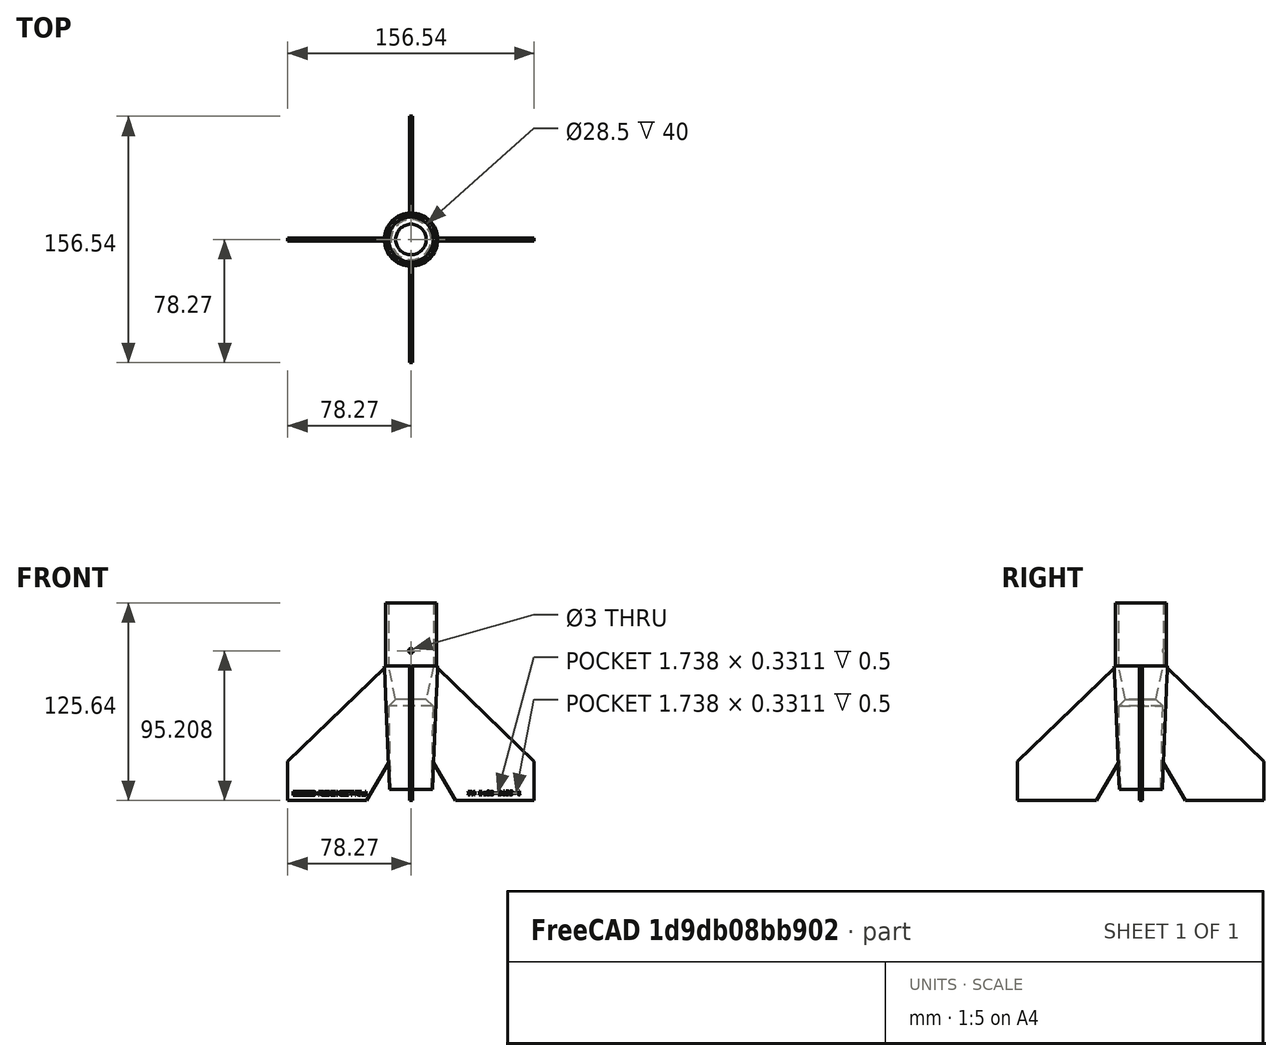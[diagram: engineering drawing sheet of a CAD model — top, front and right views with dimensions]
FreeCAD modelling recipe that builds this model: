
FCSTD DOCUMENT  (FreeCAD 0.20R29603 (Git))
Label: Ez3D-2455-4
License: All rights reserved
LicenseURL: http://en.wikipedia.org/wiki/All_rights_reserved
objects: Sketcher::SketchObject×3, Part::Part2DObjectPython×2, PartDesign::Pocket×2, PartDesign::Revolution×1, PartDesign::Pad×1, PartDesign::PolarPattern×1, Mesh::Feature×1, PartDesign::Plane×1, PartDesign::Hole×1, PartDesign::Body×1
note: 18 computed .brp shape members not serialized (recipe doc carries the construction recipe); baked Part::Feature solids carry a one-line shape summary decoded from their .brp

FEATURE [Sketcher::SketchObject] Sketch  label="Motor Mount"
  FullyConstrained = false
  MapMode = 5
  Placement = pos=(0,0,0) rot=(1,0,0;1.5708rad)
  Support = -> [XZ_Plane]
  sketch-geometry (9):
    g0: LineSegment StartX=12.7 StartY=7 StartZ=0 EndX=13.7 EndY=7 EndZ=0
    g1: LineSegment StartX=13.7 StartY=7 StartZ=0 EndX=16.95 EndY=85.6405 EndZ=0
    g2: LineSegment StartX=9.7 StartY=64.3 StartZ=0 EndX=14 EndY=60 EndZ=0
    g3: LineSegment StartX=14 StartY=60 StartZ=0 EndX=12.7 EndY=7 EndZ=0
    g4: LineSegment StartX=14.25 StartY=125.64 StartZ=0 EndX=14.25 EndY=85.6405 EndZ=0
    g5: LineSegment StartX=14.25 StartY=85.6405 StartZ=0 EndX=9.7 EndY=64.3 EndZ=0
    g6: LineSegment StartX=16.95 StartY=85.6405 StartZ=0 EndX=16.25 EndY=85.6405 EndZ=0
    g7: LineSegment StartX=16.25 StartY=85.6405 StartZ=0 EndX=16.25 EndY=125.64 EndZ=0
    g8: LineSegment StartX=16.25 StartY=125.64 StartZ=0 EndX=14.25 EndY=125.64 EndZ=0
  constraints (26):
    c: Coincident(g0,g1)
    c: Coincident(g2,g3)
    c: Coincident(g3,g0)
    c: DistanceX(g0,g0) = 1
    c: DistanceX(g-1,g0) = 12.7
    c: DistanceY(g0,g2) = 53
    c: Angle(g2) = -0.785398
    c: Vertical(g4)
    c: Coincident(g4,g5)
    c: Coincident(g6,g7)
    c: Vertical(g7)
    c: Coincident(g7,g8)
    c: Coincident(g8,g4)
    c: Horizontal(g8)
    c: Horizontal(g6)
    c: DistanceX(g-1,g7) = 16.25
    c: DistanceX(g8,g8) = 2
    c: Horizontal(g4,g6)
    c: DistanceY(g4,g4) = 40
    c: DistanceX(g6,g6) = 0.7
    c: Coincident(g5,g2)
    c: Coincident(g1,g6)
    c: DistanceX(g-1,g2) = 9.7
    c: DistanceX(g-1,g2) = 14
    c: DistanceY(g-1,g0) = 7
    c: Horizontal(g0)
FEATURE [PartDesign::Revolution] Revolution  label="Motor Mount001"
  Angle = 360
  Axis = (0,-2e-16,1)
  Base = (0,0,0)
  Placement = pos=(0,0,0) rot=(1,0,0;1.5708rad)
  Profile = -> Sketch
  ReferenceAxis = -> Sketch [V_Axis]
  Reversed = true
FEATURE [Sketcher::SketchObject] Sketch001  label="Fin"
  FullyConstrained = false
  MapMode = 5
  Placement = pos=(0,0,0) rot=(1,0,0;1.5708rad)
  Support = -> [XZ_Plane]
  sketch-geometry (5):
    g0: LineSegment StartX=28.266 StartY=0 StartZ=0 EndX=78.266 EndY=0 EndZ=0
    g1: LineSegment StartX=78.266 StartY=0 StartZ=0 EndX=78.266 EndY=25 EndZ=0
    g2: LineSegment StartX=78.266 StartY=25 StartZ=0 EndX=16 EndY=85 EndZ=0
    g3: LineSegment StartX=16 StartY=85 StartZ=0 EndX=13.5 EndY=25.5754 EndZ=0
    g4: LineSegment StartX=13.5 StartY=25.5754 StartZ=0 EndX=28.266 EndY=0 EndZ=0
  constraints (13):
    c: Coincident(g0,g1)
    c: Coincident(g1,g2)
    c: Vertical(g1)
    c: Coincident(g2,g3)
    c: Coincident(g3,g4)
    c: Coincident(g0,g4)
    c: DistanceX(g-1,g2) = 16
    c: Angle(g4) = -1.0472
    c: DistanceX(g0,g0) = 50
    c: DistanceY(g1,g1) = 25
    c: DistanceY(g1,g2) = 60
    c: Tangent(g0,g-1)
    c: DistanceX(g-1,g3) = 13.5
FEATURE [PartDesign::Pad] Pad  label="Fin001"
  BaseFeature = -> Revolution
  Direction = (0,-1,-2e-16)
  Length = 2
  Length2 = 100
  Midplane = true
  Placement = pos=(0,0,0) rot=(1,0,0;1.5708rad)
  Profile = -> Sketch001
  Type = 0
FEATURE [PartDesign::PolarPattern] PolarPattern  label="Fins"
  Angle = 360
  Axis = -> Z_Axis
  BaseFeature = -> Pad
  Occurrences = 4
  Originals = -> [Pad]
  Placement = pos=(0,0,0) rot=(1,0,0;1.5708rad)
FEATURE [Mesh::Feature] Thread_30x2_12p7Rad_10mmTall  label="Thread-M30x2-12.7radius-10mmTall"
FEATURE [PartDesign::Plane] DatumPlane
  Length = 187.244
  MapMode = 5
  Placement = pos=(0,-1,0) rot=(1,0,0;1.5708rad)
  ResizeMode = 0
  Support = -> [PolarPattern]
  Width = 181.352
FEATURE [Sketcher::SketchObject] Sketch002
  FullyConstrained = false
  MapMode = 5
  Placement = pos=(0,-1,0) rot=(1,0,0;1.5708rad)
  Support = -> [DatumPlane]
  sketch-geometry (1):
    g0: Circle CenterX=0 CenterY=95.2082 CenterZ=0 NormalX=0 NormalY=0 NormalZ=1 AngleXU=0 Radius=2.25662
  constraints (1):
    c: PointOnObject(g0,g-2)
FEATURE [PartDesign::Hole] Hole
  BaseFeature = -> PolarPattern
  CustomThreadClearance = 0
  Depth = 25
  DepthType = 0
  Diameter = 3
  DrillForDepth = false
  DrillPoint = 1
  DrillPointAngle = 118
  HoleCutCountersinkAngle = 90
  HoleCutCustomValues = false
  HoleCutDepth = 0
  HoleCutDiameter = 6.1
  HoleCutType = 0
  ModelThread = false
  Placement = pos=(0,0,0) rot=(1,0,0;1.5708rad)
  Profile = -> Sketch002
  Tapered = false
  TaperedAngle = 90
  ThreadClass = 0
  ThreadDepth = 25
  ThreadDepthType = 0
  ThreadDirection = 0
  ThreadFit = 0
  ThreadSize = 0
  ThreadType = 0
  Threaded = false
  UseCustomThreadClearance = false
FEATURE [Part::Part2DObjectPython] ShapeString  label="Logo"  # Draft 2D object (typed FeaturePython)
  FontFile = <path>
  MakeFace = true
  Placement = pos=(-75,-1,3.273) rot=(1,0,0;1.5708rad)
  Size = 1.5
  String = Ez3D Rocketry
  Tracking = 0
FEATURE [Part::Part2DObjectPython] ShapeString001  label="PN"  # Draft 2D object (typed FeaturePython)
  FontFile = <path>
  MakeFace = true
  Placement = pos=(36,-1,3.598) rot=(1,0,0;1.5708rad)
  Size = 3
  String = PN Ez3D-2455-4
  Tracking = 0
FEATURE [PartDesign::Pocket] Pocket
  BaseFeature = -> Hole
  Direction = (0,1,0)
  Length = 0.5
  Length2 = 5
  Placement = pos=(0,0,0) rot=(1,0,0;1.5708rad)
  Profile = -> ShapeString
  ReferenceAxis = -> ShapeString [N_Axis]
  Type = 0
FEATURE [PartDesign::Pocket] Pocket001
  BaseFeature = -> Pocket
  Direction = (0,1,0)
  Length = 0.5
  Length2 = 5
  Placement = pos=(0,0,0) rot=(1,0,0;1.5708rad)
  Profile = -> ShapeString001
  ReferenceAxis = -> ShapeString001 [N_Axis]
  Type = 0
FEATURE [PartDesign::Body] Body
  Group = -> [Sketch,Revolution,Sketch001,Pad,PolarPattern,DatumPlane,Sketch002,Hole,ShapeString,ShapeString001,Pocket,Pocket001]
  Origin = -> Origin
  Tip = -> Pocket001
note: 2 file-system paths scrubbed to <path> (originals preserved in the JSON sidecar)
